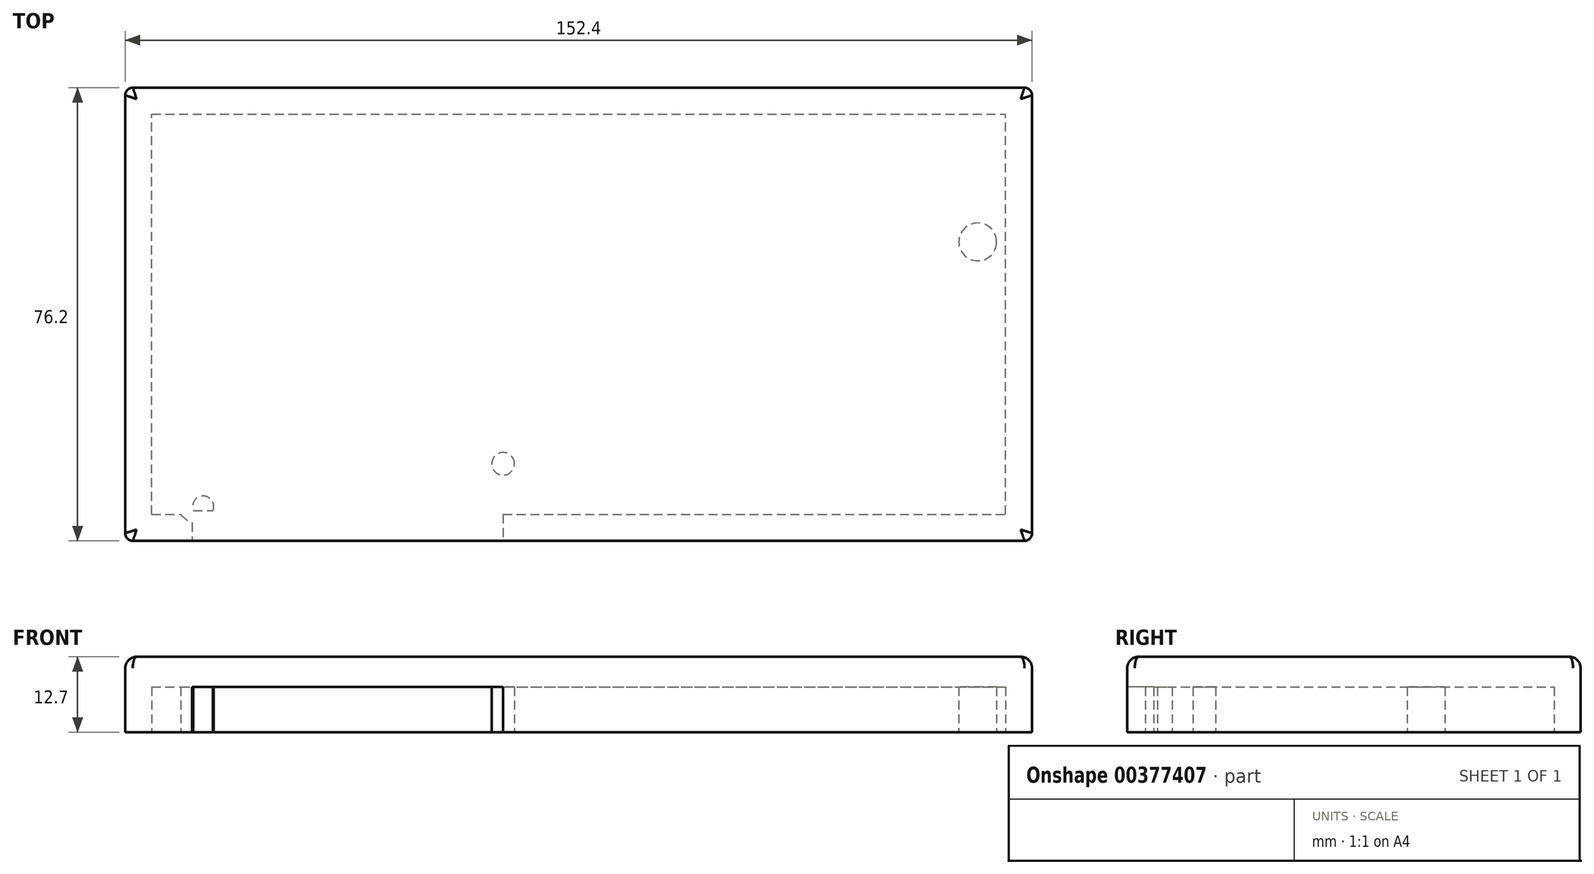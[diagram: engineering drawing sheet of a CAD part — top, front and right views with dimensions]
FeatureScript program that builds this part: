
annotation { "Feature Type Name" : "Feature", "Feature Type Description" : "" }
export const myFeature = defineFeature(function(context is Context, id is Id, definition is map)
    precondition{}
    {
        {
            var Q0;
            Q0=qCreatedBy(makeId("Top.planeOp"),FACE);
            var sketch = newSketch(context, id + "F0", { "sketchPlane" : qUnion([Q0])});
            skLineSegment(sketch, "E0.bottom", {"start": v(47.62, 23.81) * mm, "end": v(-47.63, 23.81) * mm});
            skLineSegment(sketch, "E0.top", {"start": v(15.88, -23.81) * mm, "end": v(-47.62, -23.81) * mm});
            skLineSegment(sketch, "E0.left", {"start": v(47.62, 23.81) * mm, "end": v(47.63, -11.11) * mm});
            skLineSegment(sketch, "E0.right", {"start": v(-47.63, 23.81) * mm, "end": v(-47.62, -23.81) * mm});
            skPoint(sketch, "E0.middle", {"position": v(0, 0) * mm});
            skPoint(sketch, "E1", {"position": v(15.88, -23.81) * mm});
            skPoint(sketch, "E2", {"position": v(47.63, -11.11) * mm});
            skLineSegment(sketch, "E3", {"start": v(15.88, -23.81) * mm, "end": v(47.63, -11.11) * mm});
            skPoint(sketch, "E4", {"position": v(-42.86, -25.4) * mm});
            skPoint(sketch, "E5", {"position": v(-1.59, -25.4) * mm});
            skLineSegment(sketch, "E6", {"start": v(-42.86, -25.4) * mm, "end": v(-1.59, -25.4) * mm});
            skPoint(sketch, "E7", {"position": v(-1.59, -36.51) * mm});
            skPoint(sketch, "E8", {"position": v(-53.97, -36.51) * mm});
            skLineSegment(sketch, "E9", {"start": v(-53.97, -36.51) * mm, "end": v(-1.59, -36.51) * mm});
            skLineSegment(sketch, "E10", {"start": v(-1.59, -25.4) * mm, "end": v(-1.59, -36.51) * mm});
            skLineSegment(sketch, "E11", {"start": v(-42.86, -25.4) * mm, "end": v(-53.97, -36.51) * mm});
            skArc(sketch, "E12", {"start": v(-1.59, -36.51) * mm, "mid": v(3.97, -30.96) * mm, "end": v(-1.59, -25.4) * mm});
            skPoint(sketch, "E13", {"position": v(-44.45, -36.51) * mm});
            skArc(sketch, "E14", {"start": v(-53.97, -36.51) * mm, "mid": v(-49.21, -41.28) * mm, "end": v(-44.45, -36.51) * mm});
            skLineSegment(sketch, "E15.bottom", {"start": v(-57.15, 25.4) * mm, "end": v(36.51, 25.4) * mm});
            skLineSegment(sketch, "E15.left", {"start": v(-57.15, 25.4) * mm, "end": v(-57.15, 7.99) * mm});
            skLineSegment(sketch, "E15.right", {"start": v(36.51, 25.4) * mm, "end": v(36.51, 7.99) * mm});
            skPoint(sketch, "E15.middle", {"position": v(-10.32, 16.7) * mm});
            skLineSegment(sketch, "E16", {"start": v(36.51, 7.99) * mm, "end": v(-57.15, 7.99) * mm});
            skPoint(sketch, "E17", {"position": v(47.63, 6.35) * mm});
            skPoint(sketch, "E18", {"position": v(60.32, 6.35) * mm});
            skLineSegment(sketch, "E19.bottom", {"start": v(47.62, 25.4) * mm, "end": v(73.03, 25.4) * mm});
            skLineSegment(sketch, "E19.top", {"start": v(47.63, -12.7) * mm, "end": v(73.03, -12.7) * mm});
            skLineSegment(sketch, "E19.left", {"start": v(47.63, 25.4) * mm, "end": v(47.63, -12.7) * mm});
            skLineSegment(sketch, "E19.right", {"start": v(73.03, 25.4) * mm, "end": v(73.03, -12.7) * mm});
            skPoint(sketch, "E20", {"position": v(73.03, -4.76) * mm});
            skPoint(sketch, "E21", {"position": v(73.03, 17.46) * mm});
            skPoint(sketch, "E22", {"position": v(84.93, 6.35) * mm});
            skPoint(sketch, "E23", {"position": v(84.93, 10.72) * mm});
            skPoint(sketch, "E24", {"position": v(84.93, 1.98) * mm});
            skLineSegment(sketch, "E25", {"start": v(84.93, 10.72) * mm, "end": v(84.93, 1.98) * mm});
            skLineSegment(sketch, "E26", {"start": v(84.93, 10.72) * mm, "end": v(73.03, 17.46) * mm});
            skLineSegment(sketch, "E27", {"start": v(84.93, 1.98) * mm, "end": v(73.03, -4.76) * mm});
            skPoint(sketch, "E28", {"position": v(80.96, 6.35) * mm});
            skPoint(sketch, "E28.positionSnap0", {"position": v(73.03, 6.35) * mm});
            skCircle(sketch, "E29", {"center": v(80.96, 6.35) * mm, "radius": 3.18 * mm});
            skSolve(sketch);
        }
        {
            var Q0;
            Q0=qCreatedBy(makeId("Top.planeOp"),FACE);
            var sketch = newSketch(context, id + "F1", { "sketchPlane" : qUnion([Q0])});
            skLineSegment(sketch, "E30.bottom", {"start": v(90.1, 32.3) * mm, "end": v(-62.3, 32.3) * mm});
            skLineSegment(sketch, "E30.top", {"start": v(90.1, -43.9) * mm, "end": v(-62.3, -43.9) * mm});
            skLineSegment(sketch, "E30.left", {"start": v(90.1, 32.3) * mm, "end": v(90.1, -43.9) * mm});
            skLineSegment(sketch, "E30.right", {"start": v(-62.3, 32.3) * mm, "end": v(-62.3, -43.9) * mm});
            skPoint(sketch, "E30.middle", {"position": v(0, 0) * mm});
            skPoint(sketch, "E31", {"position": v(-57.15, 25.4) * mm});
            skPoint(sketch, "E32", {"position": v(84.93, 6.35) * mm});
            skPoint(sketch, "E33", {"position": v(-53.97, -36.51) * mm});
            skPoint(sketch, "E34", {"position": v(13.9, 25.4) * mm});
            skPoint(sketch, "E35", {"position": v(13.9, 32.3) * mm});
            skPoint(sketch, "E36", {"position": v(-49.21, -36.51) * mm});
            skPoint(sketch, "E37", {"position": v(-49.21, -41.28) * mm});
            skPoint(sketch, "E38.center.orphan", {"position": v(1.34, -30.96) * mm});
            skPoint(sketch, "E39.center.orphan", {"position": v(-49.21, -38.72) * mm});
            skPoint(sketch, "E40.center.orphan", {"position": v(80.96, 6.35) * mm});
            skSolve(sketch);
        }
        {
            var Q0;
            Q0 = qSketchRegion(id + "F1", true);
            extrude(context, id + "F2", {"entities" : qUnion([Q0]), "depth" : 12.7 * mm});
        }
        {
            var Q0;
            Q0=makeQuery(id+"F2.opExtrude","SWEPT_EDGE",EDGE,{"disambiguationData":[OSD([sQuery(id+"F1.wireOp",EDGE,"E30.top"),sQuery(id+"F1.wireOp",EDGE,"E30.left")])]});
            var Q1;
            Q1=makeQuery(id+"F2.opExtrude","SWEPT_EDGE",EDGE,{"disambiguationData":[OSD([sQuery(id+"F1.wireOp",EDGE,"E30.top"),sQuery(id+"F1.wireOp",EDGE,"E30.right")])]});
            var Q2;
            Q2=makeQuery(id+"F2.opExtrude","SWEPT_EDGE",EDGE,{"disambiguationData":[OSD([sQuery(id+"F1.wireOp",EDGE,"E30.bottom"),sQuery(id+"F1.wireOp",EDGE,"E30.left")])]});
            var Q3;
            Q3=makeQuery(id+"F2.opExtrude","SWEPT_EDGE",EDGE,{"disambiguationData":[OSD([sQuery(id+"F1.wireOp",EDGE,"E30.bottom"),sQuery(id+"F1.wireOp",EDGE,"E30.right")])]});
            fillet(context, id + "F3", {"entities" : qUnion([Q0, Q1, Q2, Q3]), "radius" : 1.27 * mm, "tangentPropagation" : true, "allowEdgeOverflow" : false});
        }
        {
            var Q0;
            Q0 = qSketchRegion(id + "F0", true);
            var sketch = newSketch(context, id + "F4", { "sketchPlane" : qUnion([Q0])});
            skLineSegment(sketch, "E41.bottom", {"start": v(-57.86, -39.46) * mm, "end": v(-52.95, -39.46) * mm});
            skLineSegment(sketch, "E41.top", {"start": v(-57.86, 27.85) * mm, "end": v(85.65, 27.85) * mm});
            skLineSegment(sketch, "E41.left", {"start": v(-57.86, -39.46) * mm, "end": v(-57.86, 27.85) * mm});
            skLineSegment(sketch, "E41.right", {"start": v(85.65, -39.46) * mm, "end": v(85.65, 27.85) * mm});
            skPoint(sketch, "E42", {"position": v(-53.97, -36.51) * mm});
            skPoint(sketch, "E43", {"position": v(-44.45, -36.51) * mm});
            skArc(sketch, "E44", {"start": v(-52.95, -39.46) * mm, "mid": v(-49.21, -41.28) * mm, "end": v(-45.47, -39.46) * mm});
            skLineSegment(sketch, "E45.trimOffspring", {"start": v(-45.47, -39.46) * mm, "end": v(85.65, -39.46) * mm});
            skCircle(sketch, "E46", {"center": v(80.96, 6.35) * mm, "radius": 3.18 * mm});
            skCircle(sketch, "E47", {"center": v(1.2, -30.96) * mm, "radius": 1.9 * mm});
            skCircle(sketch, "E48", {"center": v(-49.21, -38.14) * mm, "radius": 1.78 * mm});
            skPoint(sketch, "E49", {"position": v(-51.1, -43.9) * mm});
            skPoint(sketch, "E50", {"position": v(1.2, -43.9) * mm});
            skArc(sketch, "E51", {"start": v(1.2, -43.9) * mm, "mid": v(-24.94, -33.43) * mm, "end": v(-51.1, -43.9) * mm});
            skPoint(sketch, "E51.third.point", {"position": v(-25.13, -33.43) * mm});
            skSolve(sketch);
        }
        {
            var Q0;
            Q0 = qSketchRegion(id + "F4", true);
            extrude(context, id + "F5", {"entities" : qUnion([Q0]), "operationType" : NewBodyOperationType.REMOVE, "depth" : 7.62 * mm});
        }
        {
            var Q0;
            {var subQ0=sQuery(id+"F1.wireOp",EDGE,"E30.right");var subQ1=sQuery(id+"F1.wireOp",EDGE,"E30.top");Q0=makeQuery(id+"F3.opFillet","BLEND_EDGE",EDGE,{"blendedFrom":[makeQuery(id+"F2.opExtrude","SWEPT_EDGE",EDGE,{"disambiguationData":[OSD([subQ1,subQ0])]}),makeQuery(id+"F2.opExtrude","CAP_FACE",FACE,{"disambiguationData":[OSD([sQuery(id+"F1.wireOp",EDGE,"E30.bottom"),subQ1,sQuery(id+"F1.wireOp",EDGE,"E30.left"),subQ0])],"isStart":false})],"blendedInto":[makeQuery(id+"F2.opExtrude","CAP_FACE",FACE,{"disambiguationData":[OSD([sQuery(id+"F1.wireOp",EDGE,"E30.bottom"),subQ1,sQuery(id+"F1.wireOp",EDGE,"E30.left"),subQ0])],"isStart":false})]});}
            var Q1;
            {var subQ0=sQuery(id+"F1.wireOp",EDGE,"E30.right");var subQ1=sQuery(id+"F1.wireOp",EDGE,"E30.bottom");Q1=makeQuery(id+"F3.opFillet","BLEND_EDGE",EDGE,{"blendedFrom":[makeQuery(id+"F2.opExtrude","SWEPT_EDGE",EDGE,{"disambiguationData":[OSD([subQ1,subQ0])]}),makeQuery(id+"F2.opExtrude","CAP_FACE",FACE,{"disambiguationData":[OSD([subQ1,sQuery(id+"F1.wireOp",EDGE,"E30.top"),sQuery(id+"F1.wireOp",EDGE,"E30.left"),subQ0])],"isStart":false})],"blendedInto":[makeQuery(id+"F2.opExtrude","CAP_FACE",FACE,{"disambiguationData":[OSD([subQ1,sQuery(id+"F1.wireOp",EDGE,"E30.top"),sQuery(id+"F1.wireOp",EDGE,"E30.left"),subQ0])],"isStart":false})]});}
            var Q2;
            Q2=makeQuery(id+"F2.opExtrude","CAP_EDGE",EDGE,{"disambiguationData":[OSD([sQuery(id+"F1.wireOp",EDGE,"E30.top")])],"isStart":false});
            var Q3;
            Q3=makeQuery(id+"F2.opExtrude","CAP_EDGE",EDGE,{"disambiguationData":[OSD([sQuery(id+"F1.wireOp",EDGE,"E30.right")])],"isStart":false});
            var Q4;
            {var subQ0=sQuery(id+"F1.wireOp",EDGE,"E30.left");var subQ1=sQuery(id+"F1.wireOp",EDGE,"E30.bottom");Q4=makeQuery(id+"F3.opFillet","BLEND_EDGE",EDGE,{"blendedFrom":[makeQuery(id+"F2.opExtrude","SWEPT_EDGE",EDGE,{"disambiguationData":[OSD([subQ1,subQ0])]}),makeQuery(id+"F2.opExtrude","CAP_FACE",FACE,{"disambiguationData":[OSD([subQ1,sQuery(id+"F1.wireOp",EDGE,"E30.top"),subQ0,sQuery(id+"F1.wireOp",EDGE,"E30.right")])],"isStart":false})],"blendedInto":[makeQuery(id+"F2.opExtrude","CAP_FACE",FACE,{"disambiguationData":[OSD([subQ1,sQuery(id+"F1.wireOp",EDGE,"E30.top"),subQ0,sQuery(id+"F1.wireOp",EDGE,"E30.right")])],"isStart":false})]});}
            var Q5;
            Q5=makeQuery(id+"F2.opExtrude","CAP_EDGE",EDGE,{"disambiguationData":[OSD([sQuery(id+"F1.wireOp",EDGE,"E30.left")])],"isStart":false});
            var Q6;
            Q6=makeQuery(id+"F2.opExtrude","CAP_EDGE",EDGE,{"disambiguationData":[OSD([sQuery(id+"F1.wireOp",EDGE,"E30.bottom")])],"isStart":false});
            var Q7;
            {var subQ0=sQuery(id+"F1.wireOp",EDGE,"E30.left");var subQ1=sQuery(id+"F1.wireOp",EDGE,"E30.top");Q7=makeQuery(id+"F3.opFillet","BLEND_EDGE",EDGE,{"blendedFrom":[makeQuery(id+"F2.opExtrude","SWEPT_EDGE",EDGE,{"disambiguationData":[OSD([subQ1,subQ0])]}),makeQuery(id+"F2.opExtrude","CAP_FACE",FACE,{"disambiguationData":[OSD([sQuery(id+"F1.wireOp",EDGE,"E30.bottom"),subQ1,subQ0,sQuery(id+"F1.wireOp",EDGE,"E30.right")])],"isStart":false})],"blendedInto":[makeQuery(id+"F2.opExtrude","CAP_FACE",FACE,{"disambiguationData":[OSD([sQuery(id+"F1.wireOp",EDGE,"E30.bottom"),subQ1,subQ0,sQuery(id+"F1.wireOp",EDGE,"E30.right")])],"isStart":false})]});}
            fillet(context, id + "F6", {"entities" : qUnion([Q0, Q1, Q2, Q3, Q4, Q5, Q6, Q7]), "radius" : 1.9 * mm, "tangentPropagation" : true, "allowEdgeOverflow" : false});
        }
        {
            var Q0;
            Q0=makeQuery(id+"F2.opExtrude","SWEPT_FACE",FACE,{"disambiguationData":[OSD([sQuery(id+"F1.wireOp",EDGE,"E30.top")])]});
            cPlane(context, id + "F7", {"entities" : qUnion([Q0]), "cplaneType" : CPlaneType.OFFSET, "offset" : 0 * mm, "width" : 152.4 * mm, "height" : 152.4 * mm});
        }
        {
            var Q0;
            Q0=qCreatedBy(id+"F7.planeOp",FACE);
            var sketch = newSketch(context, id + "F8", { "sketchPlane" : qUnion([Q0])});
            skLineSegment(sketch, "E52.bottom", {"start": v(-51.1, 0) * mm, "end": v(1.2, 0) * mm});
            skLineSegment(sketch, "E52.top", {"start": v(-51.1, 7.62) * mm, "end": v(1.2, 7.62) * mm});
            skLineSegment(sketch, "E52.left", {"start": v(-51.1, 0) * mm, "end": v(-51.1, 7.62) * mm});
            skLineSegment(sketch, "E52.right", {"start": v(1.2, 0) * mm, "end": v(1.2, 7.62) * mm});
            skSolve(sketch);
        }
        {
            var Q0;
            Q0 = qSketchRegion(id + "F8", true);
            extrude(context, id + "F9", {"entities" : qUnion([Q0]), "operationType" : NewBodyOperationType.REMOVE, "oppositeDirection" : true, "depth" : 5.08 * mm});
        }
    });
